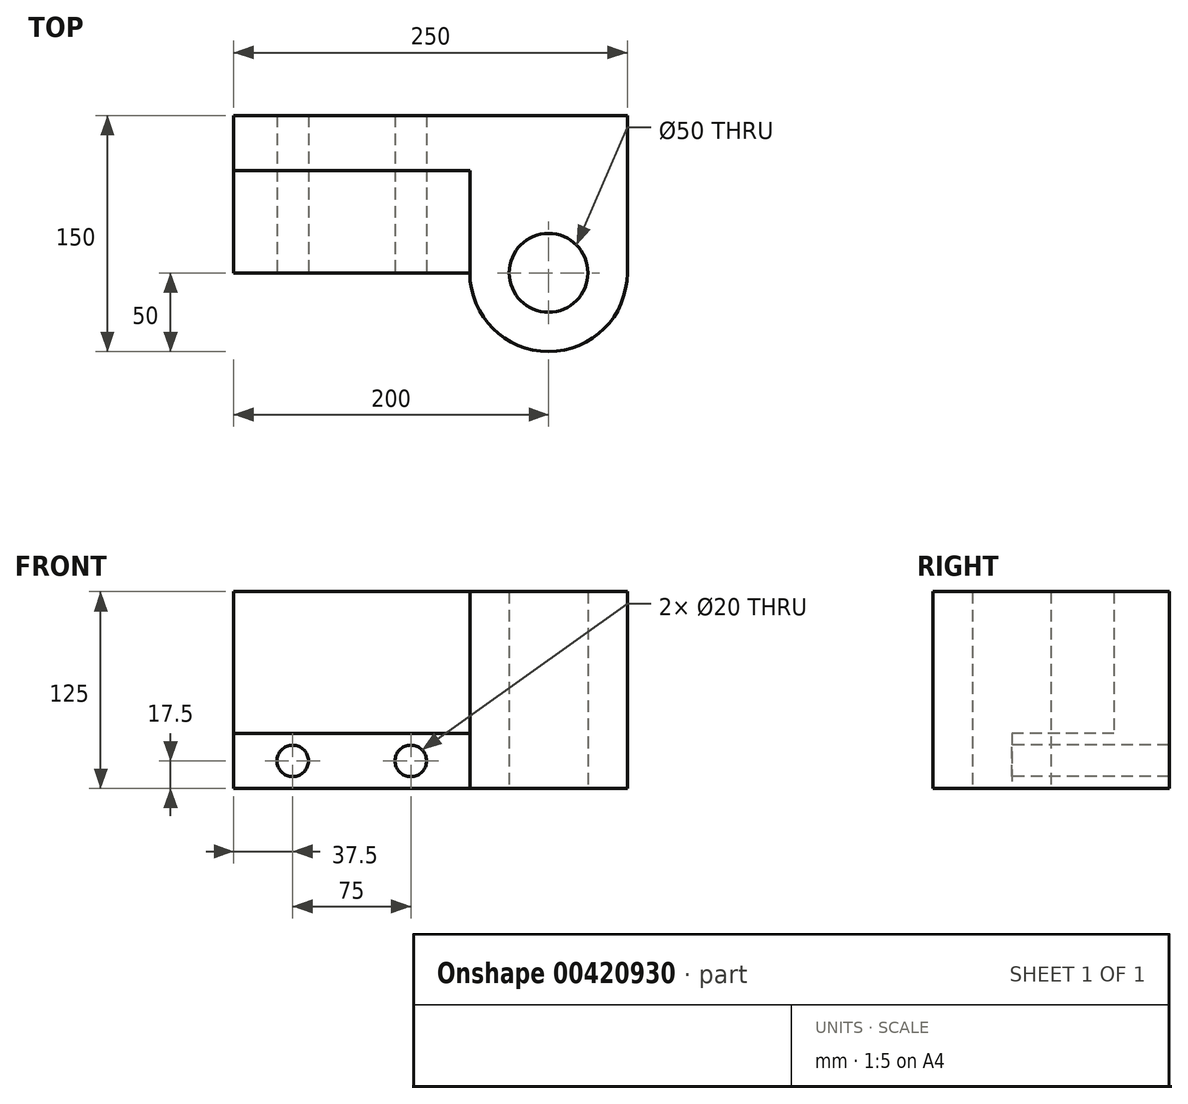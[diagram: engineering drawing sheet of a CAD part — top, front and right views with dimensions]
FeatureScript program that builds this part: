
annotation { "Feature Type Name" : "Feature", "Feature Type Description" : "" }
export const myFeature = defineFeature(function(context is Context, id is Id, definition is map)
    precondition{}
    {
        {
            var Q0;
            Q0=qCreatedBy(makeId("Top.planeOp"),FACE);
            var sketch = newSketch(context, id + "F0", { "sketchPlane" : qUnion([Q0])});
            skLineSegment(sketch, "E0.bottom", {"start": v(-125, 0) * mm, "end": v(125, 0) * mm});
            skLineSegment(sketch, "E0.top", {"start": v(-125, -100) * mm, "end": v(25, -100) * mm});
            skLineSegment(sketch, "E0.left", {"start": v(-125, 0) * mm, "end": v(-125, -100) * mm});
            skLineSegment(sketch, "E0.right", {"start": v(125, 0) * mm, "end": v(125, -100) * mm});
            skLineSegment(sketch, "E1", {"start": v(-125, -35) * mm, "end": v(25, -35) * mm});
            skLineSegment(sketch, "E2", {"start": v(25, -35) * mm, "end": v(25, -100) * mm});
            skArc(sketch, "E3", {"start": v(25, -100) * mm, "mid": v(75, -150) * mm, "end": v(125, -100) * mm});
            skCircle(sketch, "E4", {"center": v(75, -100) * mm, "radius": 25 * mm});
            skSolve(sketch);
        }
        {
            var Q0;
            {var subQ1=sQuery(id+"F0.wireOp",EDGE,"E0.bottom");Q0=makeQuery(id+"F0.imprint","IMPRINT",FACE,{"disambiguationData":[TD([[makeQuery(id+"F0.imprint","IMPRINT",EDGE,{"derivedFrom":subQ1}),-1.0]])]});}
            extrude(context, id + "F1", {"entities" : qUnion([Q0]), "flatOperationType" : FlatOperationType.REMOVE, "offsetDistance" : 25 * mm, "depth" : 125 * mm, "domain" : OperationDomain.MODEL});
        }
        {
            var Q0;
            {var subQ0=sQuery(id+"F0.wireOp",EDGE,"E0.top");Q0=makeQuery(id+"F0.imprint","IMPRINT",FACE,{"disambiguationData":[TD([[makeQuery(id+"F0.imprint","IMPRINT",EDGE,{"derivedFrom":subQ0}),1.0]])]});}
            extrude(context, id + "F2", {"entities" : qUnion([Q0]), "operationType" : NewBodyOperationType.ADD, "depth" : 35 * mm});
        }
        {
            var Q0;
            Q0=makeQuery(id+"F2.opExtrude","SWEPT_FACE",FACE,{"disambiguationData":[OSD([sQuery(id+"F0.wireOp",EDGE,"E0.top")])]});
            var sketch = newSketch(context, id + "F3", { "sketchPlane" : qUnion([Q0])});
            skCircle(sketch, "E5", {"center": v(-87.5, 17.5) * mm, "radius": 10 * mm});
            skCircle(sketch, "E6", {"center": v(-12.5, 17.5) * mm, "radius": 10 * mm});
            skSolve(sketch);
        }
        {
            var Q0;
            Q0=makeQuery(id+"F3.imprint","IMPRINT",FACE,{"disambiguationData":[TD([[makeQuery(id+"F3.imprint","IMPRINT",EDGE,{"derivedFrom":sQuery(id+"F3.wireOp",EDGE,"E5")}),1.0]])]});
            var Q1;
            Q1=makeQuery(id+"F3.imprint","IMPRINT",FACE,{"disambiguationData":[TD([[makeQuery(id+"F3.imprint","IMPRINT",EDGE,{"derivedFrom":sQuery(id+"F3.wireOp",EDGE,"E6")}),1.0]])]});
            extrude(context, id + "F4", {"entities" : qUnion([Q0, Q1]), "operationType" : NewBodyOperationType.REMOVE, "endBound" : BoundingType.THROUGH_ALL, "oppositeDirection" : true, "offsetDistance" : 25 * mm, "depth" : 25 * mm});
        }
    });
